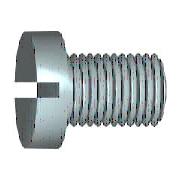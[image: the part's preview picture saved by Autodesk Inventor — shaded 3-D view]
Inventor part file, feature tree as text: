
AUTODESK INVENTOR PART (.ipt)
format: ipt  version: 2021.2 (Build 252289000, 289)  size: 175,616 bytes
history: native  units: mm (DEFAULTED — no unit token found)
features: sketch x2, other x1, extrude x1, chamfer x1, plane x1
ambient origin geometry x7: Origin, YZ Plane, XZ Plane, X Axis, Y Axis, Z Axis, Center Point
bodies: Solid1 (feature_tree)
feature tree (6):
  other  "Базовый элемент"
  sketch  "Эскиз2"
  extrude  "Паз"  Depth=40.0mm
  chamfer  "Chamfer4"  Distance=22.0mm
  plane  "Work Plane1"
  sketch  "Эскиз1"
